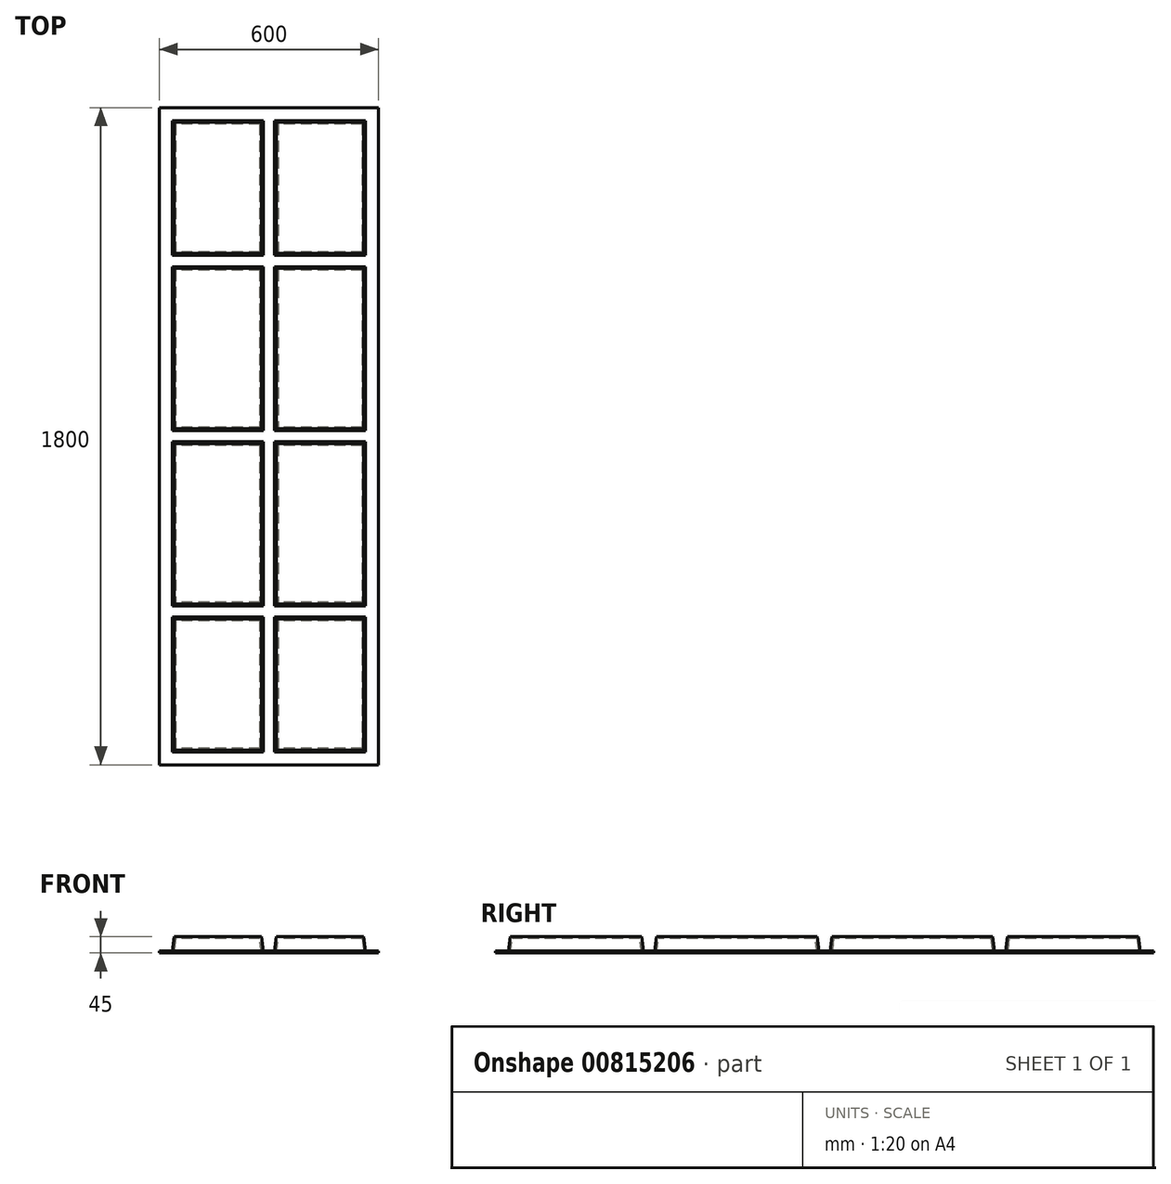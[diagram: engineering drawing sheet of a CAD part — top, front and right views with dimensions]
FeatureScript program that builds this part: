
annotation { "Feature Type Name" : "Feature", "Feature Type Description" : "" }
export const myFeature = defineFeature(function(context is Context, id is Id, definition is map)
    precondition{}
    {
        {
            var Q0;
            Q0=qCreatedBy(makeId("Front.planeOp"),FACE);
            var sketch = newSketch(context, id + "F0", { "sketchPlane" : qUnion([Q0])});
            skLineSegment(sketch, "E0", {"start": v(-170.34, 259.45) * mm, "end": v(-170.34, 254.45) * mm});
            skLineSegment(sketch, "E1.0", {"start": v(129.66, 259.45) * mm, "end": v(129.66, 254.45) * mm});
            skLineSegment(sketch, "E2", {"start": v(-170.34, 254.45) * mm, "end": v(-130.34, 254.45) * mm});
            skLineSegment(sketch, "E3", {"start": v(-125.34, 294.45) * mm, "end": v(104.66, 294.45) * mm});
            skLineSegment(sketch, "E4", {"start": v(109.66, 254.45) * mm, "end": v(129.66, 254.45) * mm});
            skLineSegment(sketch, "E5", {"start": v(-130.34, 254.45) * mm, "end": v(-125.34, 294.45) * mm});
            skLineSegment(sketch, "E6", {"start": v(104.66, 294.45) * mm, "end": v(109.66, 254.45) * mm});
            skLineSegment(sketch, "E7.1", {"start": v(-170.34, 259.45) * mm, "end": v(-134.75, 259.45) * mm});
            skLineSegment(sketch, "E8.1", {"start": v(-134.75, 259.45) * mm, "end": v(-129.75, 299.45) * mm});
            skLineSegment(sketch, "E9.0", {"start": v(114.08, 259.45) * mm, "end": v(129.66, 259.45) * mm});
            skLineSegment(sketch, "E9.1", {"start": v(109.08, 299.45) * mm, "end": v(114.08, 259.45) * mm});
            skLineSegment(sketch, "E9.2", {"start": v(-129.75, 299.45) * mm, "end": v(109.08, 299.45) * mm});
            skLineSegment(sketch, "E10.MirrorCS", {"start": v(149.66, 254.45) * mm, "end": v(129.66, 254.45) * mm});
            skLineSegment(sketch, "E11.MirrorCS", {"start": v(145.25, 259.45) * mm, "end": v(129.66, 259.45) * mm});
            skLineSegment(sketch, "E12.MirrorCS", {"start": v(150.25, 299.45) * mm, "end": v(145.25, 259.45) * mm});
            skLineSegment(sketch, "E13.MirrorCS", {"start": v(154.66, 294.45) * mm, "end": v(149.66, 254.45) * mm});
            skLineSegment(sketch, "E14.MirrorCS", {"start": v(389.08, 299.45) * mm, "end": v(150.25, 299.45) * mm});
            skLineSegment(sketch, "E15.MirrorCS", {"start": v(384.66, 294.45) * mm, "end": v(154.66, 294.45) * mm});
            skLineSegment(sketch, "E16.MirrorCS", {"start": v(394.08, 259.45) * mm, "end": v(389.08, 299.45) * mm});
            skLineSegment(sketch, "E17.MirrorCS", {"start": v(389.66, 254.45) * mm, "end": v(384.66, 294.45) * mm});
            skLineSegment(sketch, "E18.MirrorCS", {"start": v(429.66, 254.45) * mm, "end": v(389.66, 254.45) * mm});
            skLineSegment(sketch, "E19.MirrorCS", {"start": v(429.66, 259.45) * mm, "end": v(429.66, 254.45) * mm});
            skLineSegment(sketch, "E20.MirrorCS", {"start": v(429.66, 259.45) * mm, "end": v(394.08, 259.45) * mm});
            skLineSegment(sketch, "E21", {"start": v(-170.34, 254.45) * mm, "end": v(-170.34, 299.45) * mm});
            skLineSegment(sketch, "E22", {"start": v(-170.34, 299.45) * mm, "end": v(-129.75, 299.45) * mm});
            skLineSegment(sketch, "E23", {"start": v(114.08, 259.45) * mm, "end": v(145.25, 259.45) * mm});
            skLineSegment(sketch, "E24", {"start": v(109.08, 299.45) * mm, "end": v(150.25, 299.45) * mm});
            skLineSegment(sketch, "E25", {"start": v(389.08, 299.45) * mm, "end": v(429.66, 299.45) * mm});
            skLineSegment(sketch, "E26", {"start": v(429.66, 299.45) * mm, "end": v(429.66, 259.45) * mm});
            skSolve(sketch);
        }
        {
            var Q0;
            Q0=qSketchRegion(id+"F0",true);
            extrude(context, id + "F1", {"entities" : qUnion([Q0]), "oppositeDirection" : true, "depth" : 1800 * mm, "offsetDistance" : 25 * mm});
        }
        {
            var Q0;
            Q0=makeQuery(id+"F1.opExtrude","SWEPT_FACE",FACE,{"disambiguationData":[OSD([sQuery(id+"F0.wireOp",EDGE,"E21")])]});
            var sketch = newSketch(context, id + "F2", { "sketchPlane" : qUnion([Q0])});
            skLineSegment(sketch, "E27", {"start": v(0, 254.45) * mm, "end": v(0, 299.45) * mm});
            skLineSegment(sketch, "E28.0", {"start": v(-900, 254.45) * mm, "end": v(-900, 299.45) * mm});
            skLineSegment(sketch, "E29", {"start": v(-900, 299.45) * mm, "end": v(0, 299.45) * mm});
            skLineSegment(sketch, "E30.0", {"start": v(-880.04, 294.45) * mm, "end": v(-439.96, 294.45) * mm});
            skLineSegment(sketch, "E31", {"start": v(-900, 254.45) * mm, "end": v(0, 254.45) * mm});
            skLineSegment(sketch, "E32.0", {"start": v(-900, 259.45) * mm, "end": v(-884.41, 259.45) * mm});
            skLineSegment(sketch, "E33", {"start": v(-40, 254.45) * mm, "end": v(-45, 294.45) * mm});
            skLineSegment(sketch, "E34", {"start": v(-400, 254.45) * mm, "end": v(-395, 294.45) * mm});
            skLineSegment(sketch, "E35", {"start": v(-440, 254.45) * mm, "end": v(-445, 294.45) * mm});
            skLineSegment(sketch, "E36", {"start": v(-880, 254.45) * mm, "end": v(-875, 294.45) * mm});
            skLineSegment(sketch, "E37.0", {"start": v(-884.41, 259.45) * mm, "end": v(-879.41, 299.45) * mm});
            skLineSegment(sketch, "E38.trimOffspring", {"start": v(-879.37, 259.45) * mm, "end": v(-440.62, 259.45) * mm});
            skLineSegment(sketch, "E39.0", {"start": v(-404.41, 259.45) * mm, "end": v(-399.41, 299.45) * mm});
            skLineSegment(sketch, "E40.0", {"start": v(-435.59, 259.45) * mm, "end": v(-440.59, 299.45) * mm});
            skLineSegment(sketch, "E41.trimOffspring", {"start": v(-400.04, 294.45) * mm, "end": v(-39.96, 294.45) * mm});
            skLineSegment(sketch, "E42.0", {"start": v(-35.59, 259.45) * mm, "end": v(-40.59, 299.45) * mm});
            skLineSegment(sketch, "E43.trimOffspring", {"start": v(-35.59, 259.45) * mm, "end": v(0, 259.45) * mm});
            skLineSegment(sketch, "E44.trimOffspring", {"start": v(-399.38, 259.45) * mm, "end": v(-40.63, 259.45) * mm});
            skLineSegment(sketch, "E45.trimOffspring", {"start": v(-435.59, 259.45) * mm, "end": v(-404.41, 259.45) * mm});
            skLineSegment(sketch, "E46.MirrorCS", {"start": v(-900, 259.45) * mm, "end": v(-915.59, 259.45) * mm});
            skLineSegment(sketch, "E47.MirrorCS", {"start": v(-900, 254.45) * mm, "end": v(-1800, 254.45) * mm});
            skLineSegment(sketch, "E48.MirrorCS", {"start": v(-915.59, 259.45) * mm, "end": v(-920.59, 299.45) * mm});
            skLineSegment(sketch, "E49.MirrorCS", {"start": v(-920, 254.45) * mm, "end": v(-925, 294.45) * mm});
            skLineSegment(sketch, "E50.MirrorCS", {"start": v(-919.96, 294.45) * mm, "end": v(-1360.04, 294.45) * mm});
            skLineSegment(sketch, "E51.MirrorCS", {"start": v(-900, 299.45) * mm, "end": v(-1800, 299.45) * mm});
            skLineSegment(sketch, "E52.MirrorCS", {"start": v(-1364.41, 259.45) * mm, "end": v(-1395.59, 259.45) * mm});
            skLineSegment(sketch, "E53.MirrorCS", {"start": v(-1364.41, 259.45) * mm, "end": v(-1359.41, 299.45) * mm});
            skLineSegment(sketch, "E54.MirrorCS", {"start": v(-1395.59, 259.45) * mm, "end": v(-1400.59, 299.45) * mm});
            skLineSegment(sketch, "E55.MirrorCS", {"start": v(-1360, 254.45) * mm, "end": v(-1355, 294.45) * mm});
            skLineSegment(sketch, "E56.MirrorCS", {"start": v(-1400, 254.45) * mm, "end": v(-1405, 294.45) * mm});
            skLineSegment(sketch, "E57.MirrorCS", {"start": v(-1399.96, 294.45) * mm, "end": v(-1760.04, 294.45) * mm});
            skLineSegment(sketch, "E58.MirrorCS", {"start": v(-1400.63, 259.45) * mm, "end": v(-1759.38, 259.45) * mm});
            skLineSegment(sketch, "E59.MirrorCS", {"start": v(-1764.41, 259.45) * mm, "end": v(-1759.41, 299.45) * mm});
            skLineSegment(sketch, "E60.MirrorCS", {"start": v(-1760, 254.45) * mm, "end": v(-1755, 294.45) * mm});
            skLineSegment(sketch, "E61.MirrorCS", {"start": v(-1764.41, 259.45) * mm, "end": v(-1800, 259.45) * mm});
            skLineSegment(sketch, "E62.MirrorCS", {"start": v(-1800, 254.45) * mm, "end": v(-1800, 299.45) * mm});
            skSolve(sketch);
        }
        {
            var Q0;
            {var subQ0=sQuery(id+"F2.wireOp",EDGE,"E61.MirrorCS");Q0=makeQuery(id+"F2.imprint","IMPRINT",FACE,{"disambiguationData":[TD([[makeQuery(id+"F2.imprint","IMPRINT",EDGE,{"derivedFrom":subQ0}),1.0]])]});}
            extrude(context, id + "F3", {"entities" : qUnion([Q0]), "operationType" : NewBodyOperationType.REMOVE, "oppositeDirection" : true, "depth" : 800 * mm, "offsetDistance" : 25 * mm});
        }
        {
            var Q0;
            {var subQ0=sQuery(id+"F2.wireOp",EDGE,"E61.MirrorCS");Q0=makeQuery(id+"F2.imprint","IMPRINT",FACE,{"disambiguationData":[TD([[makeQuery(id+"F2.imprint","IMPRINT",EDGE,{"derivedFrom":subQ0}),-1.0]])]});}
            extrude(context, id + "F4", {"entities" : qUnion([Q0]), "operationType" : NewBodyOperationType.ADD, "oppositeDirection" : true, "depth" : 600 * mm, "offsetDistance" : 25 * mm});
        }
        {
            var Q0;
            {var subQ0=sQuery(id+"F2.wireOp",EDGE,"E59.MirrorCS");var subQ1=sQuery(id+"F2.wireOp",EDGE,"E57.MirrorCS");var subQ2=makeQuery(id+"F2.imprint","INTERSECT",VERTEX,{"derivedFrom":[subQ1,subQ0]});Q0=makeQuery(id+"F2.imprint","IMPRINT",FACE,{"disambiguationData":[TD([[makeQuery(id+"F2.imprint","IMPRINT",EDGE,{"disambiguationData":[TD([[subQ2,1.0]])],"derivedFrom":subQ1}),1.0]])]});}
            extrude(context, id + "F5", {"entities" : qUnion([Q0]), "operationType" : NewBodyOperationType.ADD, "oppositeDirection" : true, "depth" : 600 * mm, "offsetDistance" : 25 * mm});
        }
        {
            var Q0;
            {var subQ1=sQuery(id+"F2.wireOp",EDGE,"E52.MirrorCS");Q0=makeQuery(id+"F2.imprint","IMPRINT",FACE,{"disambiguationData":[TD([[makeQuery(id+"F2.imprint","IMPRINT",EDGE,{"derivedFrom":subQ1}),1.0]])]});}
            var Q1;
            {var subQ2=sQuery(id+"F2.wireOp",EDGE,"E32.0");Q1=makeQuery(id+"F2.imprint","IMPRINT",FACE,{"disambiguationData":[TD([[makeQuery(id+"F2.imprint","IMPRINT",EDGE,{"derivedFrom":subQ2}),1.0]])]});}
            var Q2;
            {var subQ1=sQuery(id+"F2.wireOp",EDGE,"E46.MirrorCS");Q2=makeQuery(id+"F2.imprint","IMPRINT",FACE,{"disambiguationData":[TD([[makeQuery(id+"F2.imprint","IMPRINT",EDGE,{"derivedFrom":subQ1}),1.0]])]});}
            var Q3;
            {var subQ4=sQuery(id+"F2.wireOp",EDGE,"E45.trimOffspring");Q3=makeQuery(id+"F2.imprint","IMPRINT",FACE,{"disambiguationData":[TD([[makeQuery(id+"F2.imprint","IMPRINT",EDGE,{"derivedFrom":subQ4}),1.0]])]});}
            var Q4;
            {var subQ6=sQuery(id+"F2.wireOp",EDGE,"E43.trimOffspring");Q4=makeQuery(id+"F2.imprint","IMPRINT",FACE,{"disambiguationData":[TD([[makeQuery(id+"F2.imprint","IMPRINT",EDGE,{"derivedFrom":subQ6}),1.0]])]});}
            extrude(context, id + "F6", {"entities" : qUnion([Q0, Q1, Q2, Q3, Q4]), "operationType" : NewBodyOperationType.REMOVE, "oppositeDirection" : true, "depth" : 800 * mm, "offsetDistance" : 25 * mm});
        }
        {
            var Q0;
            {var subQ0=sQuery(id+"F2.wireOp",EDGE,"E41.trimOffspring");var subQ1=sQuery(id+"F2.wireOp",EDGE,"E33");var subQ2=makeQuery(id+"F2.imprint","INTERSECT",VERTEX,{"derivedFrom":[subQ1,subQ0]});Q0=makeQuery(id+"F2.imprint","IMPRINT",FACE,{"disambiguationData":[TD([[makeQuery(id+"F2.imprint","IMPRINT",EDGE,{"disambiguationData":[TD([[subQ2,-1.0]])],"derivedFrom":subQ0}),-1.0]])]});}
            var Q1;
            {var subQ0=sQuery(id+"F2.wireOp",EDGE,"E43.trimOffspring");Q1=makeQuery(id+"F2.imprint","IMPRINT",FACE,{"disambiguationData":[TD([[makeQuery(id+"F2.imprint","IMPRINT",EDGE,{"derivedFrom":subQ0}),-1.0]])]});}
            var Q2;
            {var subQ0=sQuery(id+"F2.wireOp",EDGE,"E40.0");var subQ1=sQuery(id+"F2.wireOp",EDGE,"E30.0");var subQ2=makeQuery(id+"F2.imprint","INTERSECT",VERTEX,{"derivedFrom":[subQ1,subQ0]});Q2=makeQuery(id+"F2.imprint","IMPRINT",FACE,{"disambiguationData":[TD([[makeQuery(id+"F2.imprint","IMPRINT",EDGE,{"disambiguationData":[TD([[subQ2,1.0]])],"derivedFrom":subQ1}),-1.0]])]});}
            var Q3;
            {var subQ5=sQuery(id+"F2.wireOp",EDGE,"E45.trimOffspring");Q3=makeQuery(id+"F2.imprint","IMPRINT",FACE,{"disambiguationData":[TD([[makeQuery(id+"F2.imprint","IMPRINT",EDGE,{"derivedFrom":subQ5}),-1.0]])]});}
            var Q4;
            {var subQ0=sQuery(id+"F2.wireOp",EDGE,"E41.trimOffspring");var subQ1=sQuery(id+"F2.wireOp",EDGE,"E34");var subQ2=makeQuery(id+"F2.imprint","INTERSECT",VERTEX,{"derivedFrom":[subQ1,subQ0]});Q4=makeQuery(id+"F2.imprint","IMPRINT",FACE,{"disambiguationData":[TD([[makeQuery(id+"F2.imprint","IMPRINT",EDGE,{"disambiguationData":[TD([[subQ2,1.0]])],"derivedFrom":subQ0}),-1.0]])]});}
            var Q5;
            {var subQ3=sQuery(id+"F2.wireOp",EDGE,"E50.MirrorCS");var subQ5=sQuery(id+"F2.wireOp",EDGE,"E49.MirrorCS");var subQ6=makeQuery(id+"F2.imprint","INTERSECT",VERTEX,{"derivedFrom":[subQ5,subQ3]});Q5=makeQuery(id+"F2.imprint","IMPRINT",FACE,{"disambiguationData":[TD([[makeQuery(id+"F2.imprint","IMPRINT",EDGE,{"disambiguationData":[TD([[subQ6,1.0]])],"derivedFrom":subQ3}),1.0]])]});}
            var Q6;
            {var subQ7=sQuery(id+"F2.wireOp",EDGE,"E46.MirrorCS");Q6=makeQuery(id+"F2.imprint","IMPRINT",FACE,{"disambiguationData":[TD([[makeQuery(id+"F2.imprint","IMPRINT",EDGE,{"derivedFrom":subQ7}),-1.0]])]});}
            var Q7;
            {var subQ7=sQuery(id+"F2.wireOp",EDGE,"E32.0");Q7=makeQuery(id+"F2.imprint","IMPRINT",FACE,{"disambiguationData":[TD([[makeQuery(id+"F2.imprint","IMPRINT",EDGE,{"derivedFrom":subQ7}),-1.0]])]});}
            var Q8;
            {var subQ0=sQuery(id+"F2.wireOp",EDGE,"E37.0");var subQ1=sQuery(id+"F2.wireOp",EDGE,"E30.0");var subQ2=makeQuery(id+"F2.imprint","INTERSECT",VERTEX,{"derivedFrom":[subQ1,subQ0]});Q8=makeQuery(id+"F2.imprint","IMPRINT",FACE,{"disambiguationData":[TD([[makeQuery(id+"F2.imprint","IMPRINT",EDGE,{"disambiguationData":[TD([[subQ2,-1.0]])],"derivedFrom":subQ1}),-1.0]])]});}
            var Q9;
            {var subQ3=sQuery(id+"F2.wireOp",EDGE,"E57.MirrorCS");var subQ5=sQuery(id+"F2.wireOp",EDGE,"E56.MirrorCS");var subQ6=makeQuery(id+"F2.imprint","INTERSECT",VERTEX,{"derivedFrom":[subQ5,subQ3]});Q9=makeQuery(id+"F2.imprint","IMPRINT",FACE,{"disambiguationData":[TD([[makeQuery(id+"F2.imprint","IMPRINT",EDGE,{"disambiguationData":[TD([[subQ6,1.0]])],"derivedFrom":subQ3}),1.0]])]});}
            var Q10;
            {var subQ5=sQuery(id+"F2.wireOp",EDGE,"E52.MirrorCS");Q10=makeQuery(id+"F2.imprint","IMPRINT",FACE,{"disambiguationData":[TD([[makeQuery(id+"F2.imprint","IMPRINT",EDGE,{"derivedFrom":subQ5}),-1.0]])]});}
            var Q11;
            {var subQ0=sQuery(id+"F2.wireOp",EDGE,"E53.MirrorCS");var subQ1=sQuery(id+"F2.wireOp",EDGE,"E50.MirrorCS");var subQ2=makeQuery(id+"F2.imprint","INTERSECT",VERTEX,{"derivedFrom":[subQ1,subQ0]});Q11=makeQuery(id+"F2.imprint","IMPRINT",FACE,{"disambiguationData":[TD([[makeQuery(id+"F2.imprint","IMPRINT",EDGE,{"disambiguationData":[TD([[subQ2,1.0]])],"derivedFrom":subQ1}),1.0]])]});}
            extrude(context, id + "F7", {"entities" : qUnion([Q0, Q1, Q2, Q3, Q4, Q5, Q6, Q7, Q8, Q9, Q10, Q11]), "operationType" : NewBodyOperationType.ADD, "oppositeDirection" : true, "depth" : 600 * mm, "offsetDistance" : 25 * mm});
        }
        {
            var Q0;
            {var subQ0=sQuery(id+"F0.wireOp",EDGE,"E7.1");Q0=makeQuery(id+"F0.imprint","IMPRINT",FACE,{"disambiguationData":[TD([[makeQuery(id+"F0.imprint","IMPRINT",EDGE,{"derivedFrom":subQ0}),1.0]])]});}
            extrude(context, id + "F8", {"entities" : qUnion([Q0]), "operationType" : NewBodyOperationType.REMOVE, "oppositeDirection" : true, "depth" : 1900 * mm, "offsetDistance" : 25 * mm});
        }
        {
            var Q0;
            {var subQ3=sQuery(id+"F0.wireOp",EDGE,"E9.1");Q0=makeQuery(id+"F0.imprint","IMPRINT",FACE,{"disambiguationData":[TD([[makeQuery(id+"F0.imprint","IMPRINT",EDGE,{"derivedFrom":subQ3}),1.0]])]});}
            extrude(context, id + "F9", {"entities" : qUnion([Q0]), "operationType" : NewBodyOperationType.REMOVE, "oppositeDirection" : true, "depth" : 1900 * mm, "offsetDistance" : 25 * mm});
        }
        {
            var Q0;
            Q0=makeQuery(id+"F0.imprint","IMPRINT",FACE,{"disambiguationData":[TD([[makeQuery(id+"F0.imprint","IMPRINT",EDGE,{"derivedFrom":sQuery(id+"F0.wireOp",EDGE,"E16.MirrorCS")}),-1.0]])]});
            extrude(context, id + "F10", {"entities" : qUnion([Q0]), "operationType" : NewBodyOperationType.REMOVE, "oppositeDirection" : true, "depth" : 1900 * mm, "offsetDistance" : 25 * mm});
        }
        {
            var Q0;
            {var subQ4=sQuery(id+"F2.wireOp",EDGE,"E61.MirrorCS");Q0=makeQuery(id+"F2.imprint","IMPRINT",FACE,{"disambiguationData":[TD([[makeQuery(id+"F2.imprint","IMPRINT",EDGE,{"derivedFrom":subQ4}),-1.0]])]});}
            var Q1;
            {var subQ1=sQuery(id+"F2.wireOp",EDGE,"E52.MirrorCS");Q1=makeQuery(id+"F2.imprint","IMPRINT",FACE,{"disambiguationData":[TD([[makeQuery(id+"F2.imprint","IMPRINT",EDGE,{"derivedFrom":subQ1}),-1.0]])]});}
            var Q2;
            {var subQ1=sQuery(id+"F2.wireOp",EDGE,"E46.MirrorCS");Q2=makeQuery(id+"F2.imprint","IMPRINT",FACE,{"disambiguationData":[TD([[makeQuery(id+"F2.imprint","IMPRINT",EDGE,{"derivedFrom":subQ1}),-1.0]])]});}
            extrude(context, id + "F11", {"entities" : qUnion([Q0, Q1, Q2]), "operationType" : NewBodyOperationType.REMOVE, "oppositeDirection" : true, "depth" : 800 * mm, "offsetDistance" : 25 * mm});
        }
    });
